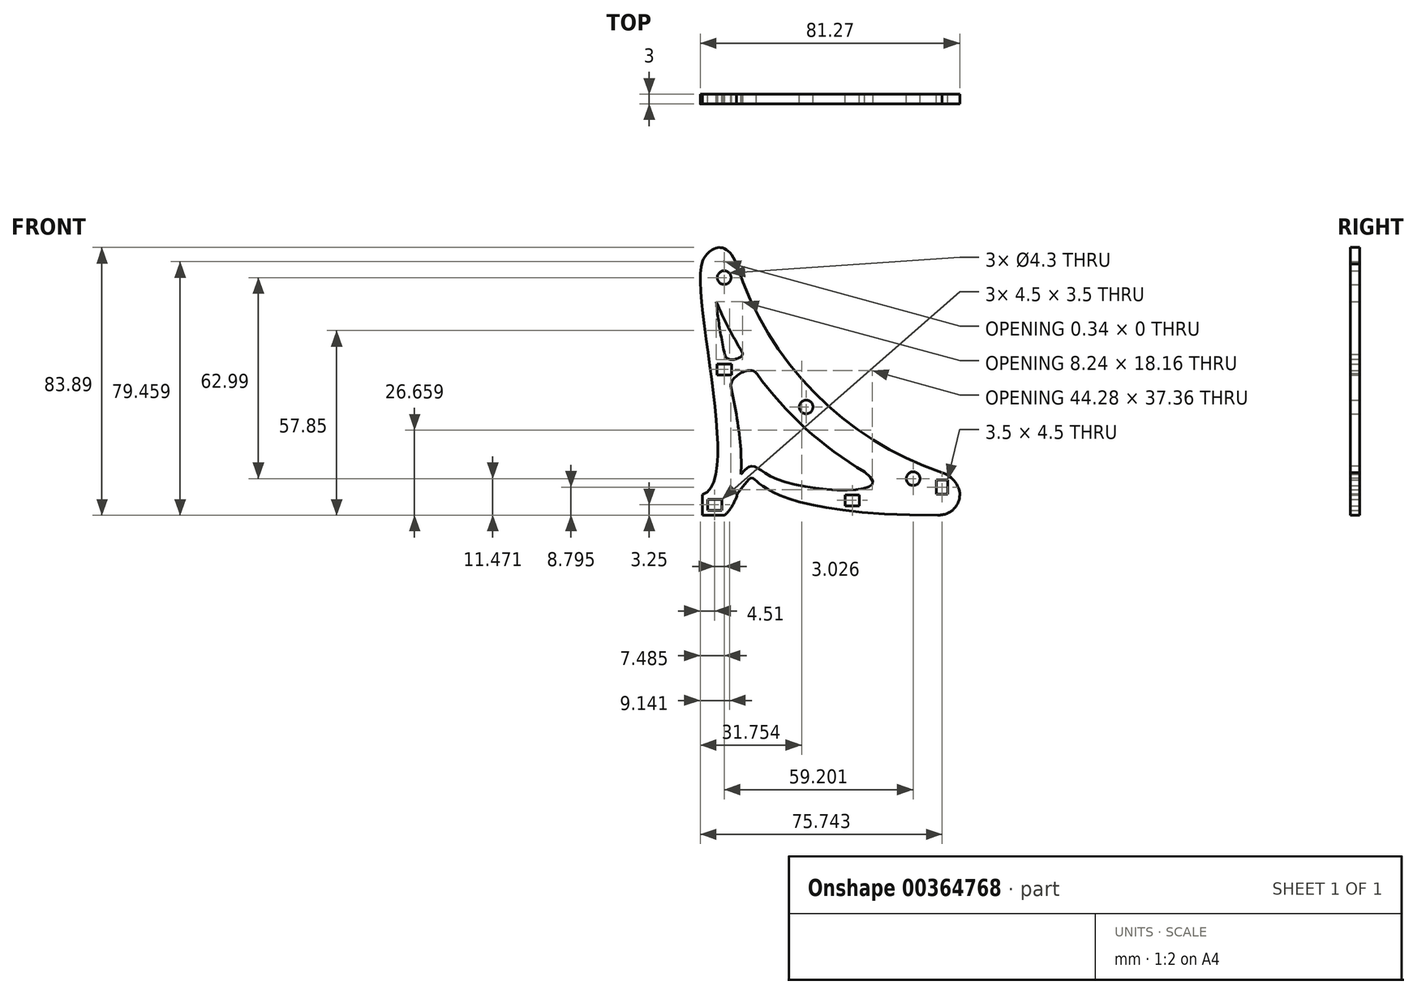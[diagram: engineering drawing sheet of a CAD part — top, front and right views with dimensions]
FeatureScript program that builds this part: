
annotation { "Feature Type Name" : "Feature", "Feature Type Description" : "" }
export const myFeature = defineFeature(function(context is Context, id is Id, definition is map)
    precondition{}
    {
        {
            var Q0;
            Q0=qCreatedBy(makeId("Front.planeOp"),FACE);
            var sketch = newSketch(context, id + "F0", { "sketchPlane" : qUnion([Q0])});
            skCircle(sketch, "E0", {"center": v(0, 0) * mm, "radius": 100 * mm, "construction": true});
            skLineSegment(sketch, "E1", {"start": v(-139.98, -110) * mm, "end": v(124.18, -110) * mm, "construction": true});
            skCircle(sketch, "E2", {"center": v(0, 0) * mm, "radius": 107 * mm, "construction": true});
            skCircle(sketch, "E3", {"center": v(-41.72, -98.53) * mm, "radius": 6.5 * mm, "construction": true});
            skLineSegment(sketch, "E4", {"start": v(0, -100) * mm, "end": v(-116.7, -100) * mm, "construction": true});
            skLineSegment(sketch, "E5", {"start": v(-115.34, -105) * mm, "end": v(71.7, -105) * mm, "construction": true});
            skCircle(sketch, "E6", {"center": v(-41.72, -98.53) * mm, "radius": 3 * mm});
            skCircle(sketch, "E7", {"center": v(0, 0) * mm, "radius": 102 * mm});
            skLineSegment(sketch, "E8", {"start": v(0, 0) * mm, "end": v(0, -123.35) * mm, "construction": true});
            skLineSegment(sketch, "E9", {"start": v(-7.34, -103.5) * mm, "end": v(11.61, -103.5) * mm, "construction": true});
            skCircle(sketch, "E10", {"center": v(0, -103.5) * mm, "radius": 2.5 * mm});
            skLineSegment(sketch, "E11", {"start": v(0, 0) * mm, "end": v(-137.34, 0) * mm, "construction": true});
            skLineSegment(sketch, "E12", {"start": v(0, 0) * mm, "end": v(-79.5, -80.36) * mm, "construction": true});
            skLineSegment(sketch, "E13", {"start": v(0, 0) * mm, "end": v(-103.96, -36.6) * mm, "construction": true});
            skCircle(sketch, "E14", {"center": v(-100.93, -35.54) * mm, "radius": 3 * mm});
            skCircle(sketch, "E15", {"center": v(-75.26, -76.06) * mm, "radius": 3 * mm});
            skCircle(sketch, "E16", {"center": v(0, 0) * mm, "radius": 112 * mm});
            skLineSegment(sketch, "E17.bottom", {"start": v(-107.76, -30.54) * mm, "end": v(-100.76, -30.54) * mm});
            skLineSegment(sketch, "E17.top", {"start": v(-107.8, -110) * mm, "end": v(-100.8, -110) * mm});
            skLineSegment(sketch, "E18.bottom", {"start": v(-107.8, -110) * mm, "end": v(-0.04, -110) * mm});
            skLineSegment(sketch, "E18.left", {"start": v(-107.8, -110) * mm, "end": v(-107.75, -103.5) * mm});
            skLineSegment(sketch, "E18.right", {"start": v(-0.04, -110) * mm, "end": v(0, -103.5) * mm});
            skCircle(sketch, "E19", {"center": v(0, -103.5) * mm, "radius": 6.5 * mm});
            skFitSpline(sketch, "E20", {"points": [v(-4.83, -99.15) * mm, v(-18.33, -103.5) * mm], "startDerivative": vector(-7.53, -7.74) * mm, "endDerivative": vector(-32.97, 0) * mm});
            skCircle(sketch, "E21", {"center": v(-100.93, -35.54) * mm, "radius": 5 * mm});
            skFitSpline(sketch, "E22", {"points": [v(-34.02, -96.16) * mm, v(-34.07, -110) * mm], "startDerivative": vector(31.1, -9.18) * mm, "endDerivative": vector(-23.87, 0) * mm});
            skFitSpline(sketch, "E23", {"points": [v(-107.76, -30.54) * mm, v(-107.75, -103.5) * mm], "startDerivative": vector(-12.24, -31.4) * mm, "endDerivative": vector(-37.86, -10.5) * mm});
            skFitSpline(sketch, "E24", {"points": [v(-100.8, -110) * mm, v(-100.76, -30.54) * mm], "startDerivative": vector(48.08, 43.13) * mm, "endDerivative": vector(33.24, 31.4) * mm});
            skFitSpline(sketch, "E25", {"points": [v(-107.76, -30.54) * mm, v(-96.2, -33.88) * mm], "startDerivative": vector(3.87, 11.05) * mm, "endDerivative": vector(10.6, -37.58) * mm});
            skFitSpline(sketch, "E26", {"points": [v(-96.78, -103.33) * mm, v(-34.07, -110) * mm], "startDerivative": vector(32.7, 42.99) * mm, "endDerivative": vector(214.65, 0) * mm});
            skFitSpline(sketch, "E27", {"points": [v(-95.7, -97.2) * mm, v(-84.06, -98.83) * mm, v(-56.9, -96.47) * mm], "startDerivative": vector(33.59, 40.14) * mm, "endDerivative": vector(-54.6, 38.62) * mm});
            skLineSegment(sketch, "E28.bottom", {"start": v(-106.15, -105) * mm, "end": v(-101.65, -105) * mm});
            skLineSegment(sketch, "E28.top", {"start": v(-106.15, -108.5) * mm, "end": v(-101.65, -108.5) * mm});
            skLineSegment(sketch, "E28.left", {"start": v(-106.15, -105) * mm, "end": v(-106.15, -108.5) * mm});
            skLineSegment(sketch, "E28.right", {"start": v(-101.65, -105) * mm, "end": v(-101.65, -108.5) * mm});
            skLineSegment(sketch, "E29.bottom", {"start": v(-103.12, -62.6) * mm, "end": v(-98.62, -62.6) * mm});
            skLineSegment(sketch, "E29.top", {"start": v(-103.12, -66.1) * mm, "end": v(-98.62, -66.1) * mm});
            skLineSegment(sketch, "E29.left", {"start": v(-103.12, -62.6) * mm, "end": v(-103.12, -66.1) * mm});
            skLineSegment(sketch, "E29.right", {"start": v(-98.62, -62.6) * mm, "end": v(-98.62, -66.1) * mm});
            skFitSpline(sketch, "E30", {"points": [v(-100.8, -59.63) * mm, v(-95.25, -58.92) * mm], "startDerivative": vector(2.48, -9.42) * mm, "endDerivative": vector(-3.2, 5.07) * mm});
            skFitSpline(sketch, "E31", {"points": [v(-98.8, -69.44) * mm, v(-90.79, -65.59) * mm], "startDerivative": vector(-1.6, 8.27) * mm, "endDerivative": vector(5.68, -8.11) * mm});
            skLineSegment(sketch, "E32.bottom", {"start": v(-63.04, -103.6) * mm, "end": v(-58.54, -103.6) * mm});
            skLineSegment(sketch, "E32.top", {"start": v(-63.04, -107.1) * mm, "end": v(-58.54, -107.1) * mm});
            skLineSegment(sketch, "E32.left", {"start": v(-63.04, -103.6) * mm, "end": v(-63.04, -107.1) * mm});
            skLineSegment(sketch, "E32.right", {"start": v(-58.54, -103.6) * mm, "end": v(-58.54, -107.1) * mm});
            skCircle(sketch, "E33", {"center": v(-41.72, -98.53) * mm, "radius": 2.15 * mm});
            skCircle(sketch, "E34", {"center": v(-75.26, -76.06) * mm, "radius": 2.15 * mm});
            skCircle(sketch, "E35", {"center": v(-100.93, -35.54) * mm, "radius": 2.15 * mm});
            skLineSegment(sketch, "E36.bottom", {"start": v(-34.42, -98.95) * mm, "end": v(-30.92, -98.95) * mm});
            skLineSegment(sketch, "E36.top", {"start": v(-34.42, -103.45) * mm, "end": v(-30.92, -103.45) * mm});
            skLineSegment(sketch, "E36.left", {"start": v(-34.42, -98.95) * mm, "end": v(-34.42, -103.45) * mm});
            skLineSegment(sketch, "E36.right", {"start": v(-30.92, -98.95) * mm, "end": v(-30.92, -103.45) * mm});
            skSolve(sketch);
        }
        {
            var Q0;
            {var subQ1=sQuery(id+"F0.wireOp",EDGE,"E16");var subQ3=sQuery(id+"F0.wireOp",EDGE,"E21");var subQ4=makeQuery(id+"F0.imprint","INTERSECT",VERTEX,{"derivedFrom":[subQ1,subQ3]});Q0=makeQuery(id+"F0.imprint","IMPRINT",FACE,{"disambiguationData":[TD([[makeQuery(id+"F0.imprint","IMPRINT",EDGE,{"disambiguationData":[TD([[subQ4,1.0]])],"derivedFrom":subQ3}),-1.0]])]});}
            var Q1;
            {var subQ4=sQuery(id+"F0.wireOp",EDGE,"E25");var subQ5=sQuery(id+"F0.wireOp",EDGE,"E7");var subQ8=makeQuery(id+"F0.imprint","INTERSECT",VERTEX,{"derivedFrom":[subQ5,subQ4]});Q1=makeQuery(id+"F0.imprint","IMPRINT",FACE,{"disambiguationData":[TD([[makeQuery(id+"F0.imprint","IMPRINT",EDGE,{"disambiguationData":[TD([[subQ8,-1.0]])],"derivedFrom":subQ5}),-1.0]])]});}
            var Q2;
            {var subQ0=sQuery(id+"F0.wireOp",EDGE,"E24");var subQ1=sQuery(id+"F0.wireOp",EDGE,"E14");var subQ2=makeQuery(id+"F0.imprint","INTERSECT",VERTEX,{"disambiguationData":[OD(0.0)],"derivedFrom":[subQ1,subQ0]});Q2=makeQuery(id+"F0.imprint","IMPRINT",FACE,{"disambiguationData":[TD([[makeQuery(id+"F0.imprint","IMPRINT",EDGE,{"disambiguationData":[TD([[subQ2,-1.0]])],"derivedFrom":subQ1}),-1.0]])]});}
            var Q3;
            {var subQ4=sQuery(id+"F0.wireOp",EDGE,"E24");var subQ7=sQuery(id+"F0.wireOp",EDGE,"E14");var subQ8=makeQuery(id+"F0.imprint","INTERSECT",VERTEX,{"disambiguationData":[OD(0.0)],"derivedFrom":[subQ7,subQ4]});Q3=makeQuery(id+"F0.imprint","IMPRINT",FACE,{"disambiguationData":[TD([[makeQuery(id+"F0.imprint","IMPRINT",EDGE,{"disambiguationData":[TD([[subQ8,1.0]])],"derivedFrom":subQ7}),-1.0]])]});}
            var Q4;
            {var subQ7=sQuery(id+"F0.wireOp",EDGE,"E18.left");Q4=makeQuery(id+"F0.imprint","IMPRINT",FACE,{"disambiguationData":[TD([[makeQuery(id+"F0.imprint","IMPRINT",EDGE,{"derivedFrom":subQ7}),-1.0]])]});}
            var Q5;
            {var subQ0=sQuery(id+"F0.wireOp",EDGE,"E21");var subQ1=sQuery(id+"F0.wireOp",EDGE,"E16");var subQ2=makeQuery(id+"F0.imprint","INTERSECT",VERTEX,{"derivedFrom":[subQ1,subQ0]});Q5=makeQuery(id+"F0.imprint","IMPRINT",FACE,{"disambiguationData":[TD([[makeQuery(id+"F0.imprint","IMPRINT",EDGE,{"disambiguationData":[TD([[subQ2,-1.0]])],"derivedFrom":subQ1}),1.0]])]});}
            var Q6;
            Q6=makeQuery(id+"F0.imprint","IMPRINT",FACE,{"disambiguationData":[TD([[makeQuery(id+"F0.imprint","IMPRINT",EDGE,{"derivedFrom":sQuery(id+"F0.wireOp",EDGE,"E6")}),-1.0]])]});
            var Q7;
            {var subQ0=sQuery(id+"F0.wireOp",EDGE,"E29.right");Q7=makeQuery(id+"F0.imprint","IMPRINT",FACE,{"disambiguationData":[TD([[makeQuery(id+"F0.imprint","IMPRINT",EDGE,{"derivedFrom":subQ0}),1.0]])]});}
            var Q8;
            {var subQ0=sQuery(id+"F0.wireOp",EDGE,"E26");Q8=makeQuery(id+"F0.imprint","IMPRINT",FACE,{"disambiguationData":[TD([[makeQuery(id+"F0.imprint","IMPRINT",EDGE,{"derivedFrom":subQ0}),1.0]])]});}
            extrude(context, id + "F1", {"entities" : qUnion([Q0, Q1, Q2, Q3, Q4, Q5, Q6, Q7, Q8]), "depth" : 3 * mm});
        }
        {
            var Q0;
            Q0=makeQuery(id+"F0.imprint","IMPRINT",FACE,{"disambiguationData":[TD([[makeQuery(id+"F0.imprint","IMPRINT",EDGE,{"derivedFrom":sQuery(id+"F0.wireOp",EDGE,"E6")}),1.0]])]});
            var Q1;
            Q1=makeQuery(id+"F0.imprint","IMPRINT",FACE,{"disambiguationData":[TD([[makeQuery(id+"F0.imprint","IMPRINT",EDGE,{"derivedFrom":sQuery(id+"F0.wireOp",EDGE,"E15")}),1.0]])]});
            var Q2;
            Q2=makeQuery(id+"F0.imprint","IMPRINT",FACE,{"disambiguationData":[TD([[makeQuery(id+"F0.imprint","IMPRINT",EDGE,{"derivedFrom":sQuery(id+"F0.wireOp",EDGE,"E35")}),-1.0]])]});
            var Q3;
            {var subQ0=sQuery(id+"F0.wireOp",EDGE,"E24");var subQ1=sQuery(id+"F0.wireOp",EDGE,"E14");var subQ2=makeQuery(id+"F0.imprint","INTERSECT",VERTEX,{"disambiguationData":[OD(0.0)],"derivedFrom":[subQ1,subQ0]});Q3=makeQuery(id+"F0.imprint","IMPRINT",FACE,{"disambiguationData":[TD([[makeQuery(id+"F0.imprint","IMPRINT",EDGE,{"disambiguationData":[TD([[subQ2,1.0]])],"derivedFrom":subQ1}),1.0]])]});}
            extrude(context, id + "F2", {"entities" : qUnion([Q0, Q1, Q2, Q3]), "operationType" : NewBodyOperationType.ADD, "depth" : 3 * mm});
        }
    });
